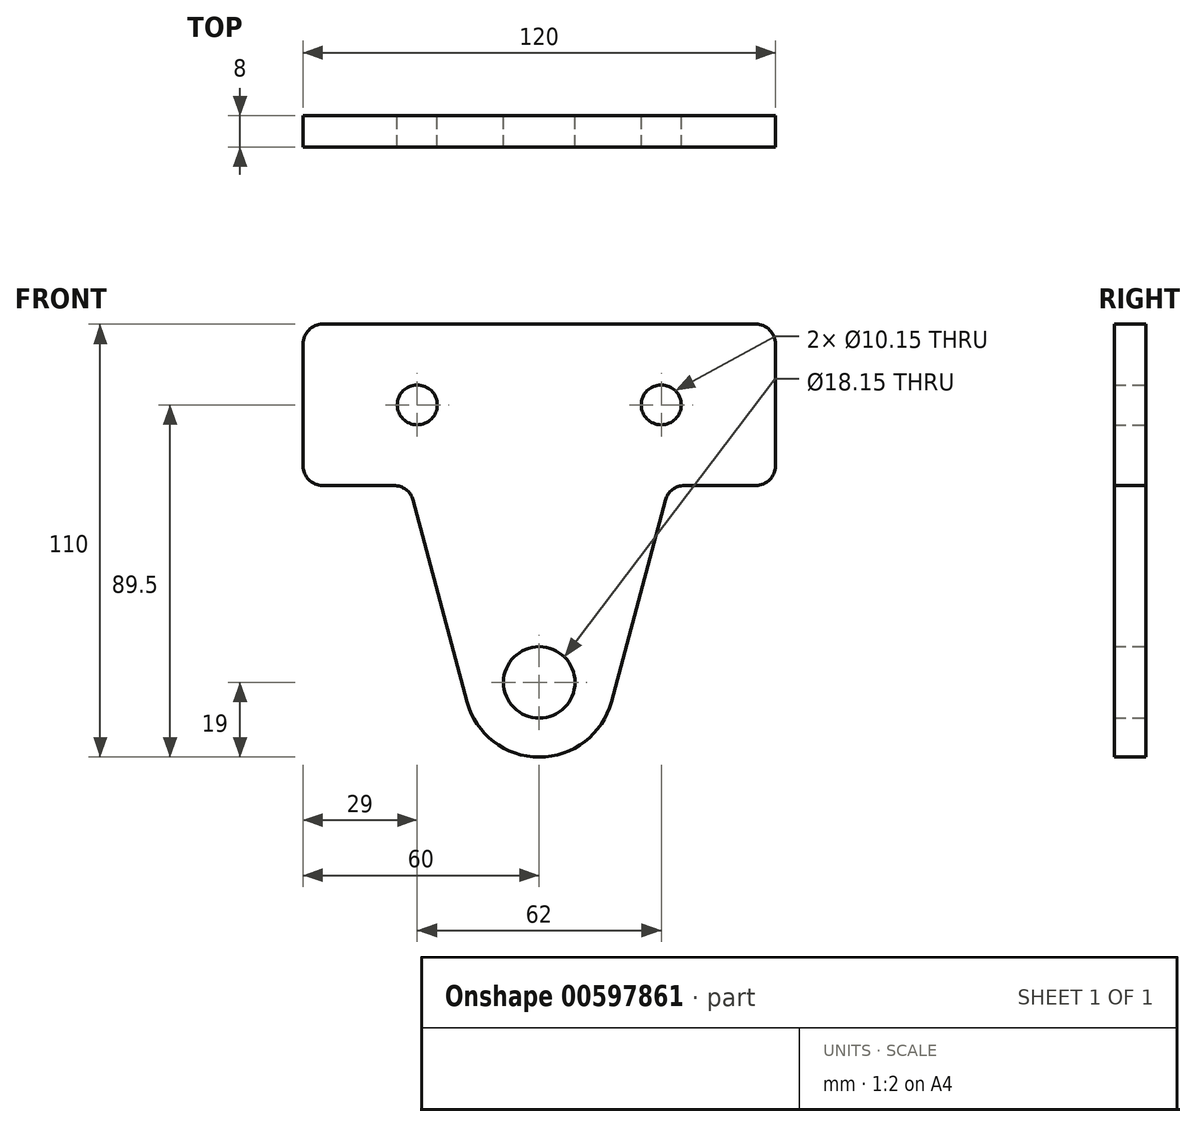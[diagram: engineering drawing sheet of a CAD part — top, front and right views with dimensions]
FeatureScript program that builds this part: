
annotation { "Feature Type Name" : "Feature", "Feature Type Description" : "" }
export const myFeature = defineFeature(function(context is Context, id is Id, definition is map)
    precondition{}
    {
        {
            var Q0;
            Q0=qCreatedBy(makeId("Front.planeOp"),FACE);
            var sketch = newSketch(context, id + "F0", { "sketchPlane" : qUnion([Q0])});
            skLineSegment(sketch, "E0", {"start": v(0, 0) * mm, "end": v(0, 9.92) * mm});
            skLineSegment(sketch, "E1", {"start": v(0, 110) * mm, "end": v(-55, 110) * mm});
            skLineSegment(sketch, "E2", {"start": v(-60, 105) * mm, "end": v(-60, 74) * mm});
            skLineSegment(sketch, "E3", {"start": v(-55, 69) * mm, "end": v(-36.9, 69) * mm});
            skArc(sketch, "E4", {"start": v(-18.35, 14.08) * mm, "mid": v(-11.57, 3.93) * mm, "end": v(0, 0) * mm});
            skLineSegment(sketch, "E5", {"start": v(-18.35, 14.08) * mm, "end": v(-32.07, 65.3) * mm});
            skArc(sketch, "E6", {"start": v(0, 28.07) * mm, "mid": v(-9.07, 19) * mm, "end": v(0, 9.92) * mm});
            skCircle(sketch, "E7", {"center": v(-31, 89.5) * mm, "radius": 5.08 * mm});
            skLineSegment(sketch, "E8.trimOffspring", {"start": v(0, 28.07) * mm, "end": v(0, 110) * mm});
            skPoint(sketch, "E9.visualSharp", {"position": v(-60, 110) * mm});
            skArc(sketch, "E9.filletArc", {"start": v(-55, 110) * mm, "mid": v(-58.54, 108.54) * mm, "end": v(-60, 105) * mm});
            skPoint(sketch, "E10.visualSharp", {"position": v(-60, 69) * mm});
            skArc(sketch, "E10.filletArc", {"start": v(-60, 74) * mm, "mid": v(-58.54, 70.46) * mm, "end": v(-55, 69) * mm});
            skPoint(sketch, "E11.visualSharp", {"position": v(-33.07, 69) * mm});
            skArc(sketch, "E11.filletArc", {"start": v(-32.07, 65.3) * mm, "mid": v(-33.86, 67.97) * mm, "end": v(-36.9, 69) * mm});
            skSolve(sketch);
        }
        {
            var Q0;
            Q0=makeQuery(id+"F0.imprint","IMPRINT",FACE,{"disambiguationData":[TD([[makeQuery(id+"F0.imprint","IMPRINT",EDGE,{"derivedFrom":sQuery(id+"F0.wireOp",EDGE,"E0")}),1.0]])]});
            extrude(context, id + "F1", {"entities" : qUnion([Q0]), "depth" : 8 * mm, "offsetDistance" : 25 * mm});
        }
        {
            var Q0;
            Q0=makeQuery(id+"F1.opExtrude","SWEPT_BODY",BODY,{"disambiguationData":[OSD([sQuery(id+"F0.wireOp",EDGE,"E0"),sQuery(id+"F0.wireOp",EDGE,"E1"),sQuery(id+"F0.wireOp",EDGE,"E2"),sQuery(id+"F0.wireOp",EDGE,"E3"),sQuery(id+"F0.wireOp",EDGE,"E4"),sQuery(id+"F0.wireOp",EDGE,"E5"),sQuery(id+"F0.wireOp",EDGE,"E6"),sQuery(id+"F0.wireOp",EDGE,"E7"),sQuery(id+"F0.wireOp",EDGE,"E8.trimOffspring"),sQuery(id+"F0.wireOp",EDGE,"E9.filletArc"),sQuery(id+"F0.wireOp",EDGE,"E10.filletArc"),sQuery(id+"F0.wireOp",EDGE,"E11.filletArc")])]});
            var Q1;
            Q1=makeQuery(id+"F1.opExtrude","SWEPT_FACE",FACE,{"disambiguationData":[OSD([sQuery(id+"F0.wireOp",EDGE,"E8.trimOffspring")])]});
            mirror(context, id + "F2", {"operationType" : NewBodyOperationType.ADD, "entities" : qUnion([Q0]), "mirrorPlane" : qUnion([Q1])});
        }
    });
